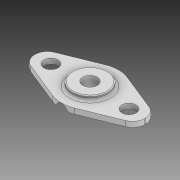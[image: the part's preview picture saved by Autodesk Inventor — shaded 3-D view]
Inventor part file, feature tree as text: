
AUTODESK INVENTOR PART (.ipt)
format: ipt  version: 2020 (Build 240168000, 168)  size: 333,824 bytes
history: native  units: mm
features: other x7, sketch x4, extrude x3, fillet x3, revolve x2, imported_body x1
ambient origin geometry x8: Origin, YZ Plane, XZ Plane, XY Plane, X Axis, Y Axis, Z Axis, Center Point
bodies: Solid1 (feature_tree)
feature tree (20):
  other  "HD_mastersketch.ipt"
  other  "Blocks"
  revolve  "Revolution1"  [1 undecoded]
  extrude  "Extrusion1"  Depth=10.0mm
  extrude  "Extrusion2"  TaperAngle=0.0deg  [1 undecoded]
  fillet  "Fillet1"  [1 undecoded]
  extrude  "Extrusion3"  Depth=1.0mm
  revolve  "Revolution2"  [1 undecoded]
  fillet  "Fillet3"  Radius=5.7mm
  fillet  "Fillet4"  Radius=5.7mm
  other  "608 bearing"
  other  "Belt"
  other  "Rotor"
  imported_body  "Base"
  sketch  "Sketch8"  dims[d1=10.0mm d24=7.0mm d25=22.0mm d26=8.0mm]
  sketch  "Sketch9"  dims[d2=90.0deg d3=5.0mm d4=10.0mm]
  sketch  "Sketch10"  dims[d5=15.0mm d6=0.0mm d7=0.0mm d8=0.0mm d9=0.0mm]
  sketch  "Sketch14"  dims[d10=7.0mm d11=4.0mm d12=2.3mm d13=5.7mm d14=5.7mm d15=0.0mm d29=1.65mm d30=3.0mm d32=10.0mm d33=1.5mm d34=90.0deg d36=4.0mm d37=2.0mm d38=1.0mm]
  other  "608 bearing:1"
  other  "608 bearing:2"
note: 4 required parameter values undecoded (feature->parameter linkage not recoverable at this tier; creation-order binding heuristic only, values carry confidence <= 0.55)